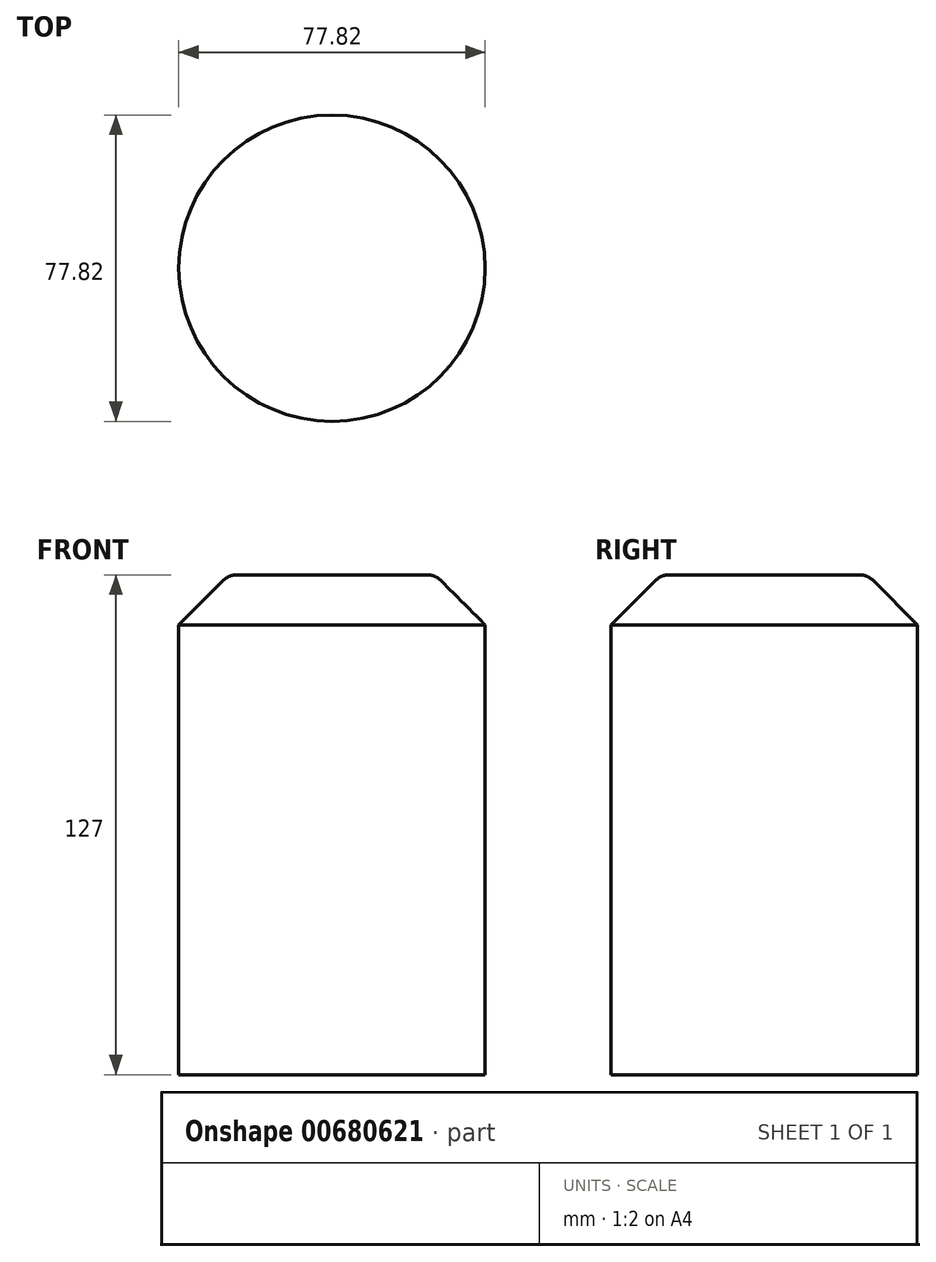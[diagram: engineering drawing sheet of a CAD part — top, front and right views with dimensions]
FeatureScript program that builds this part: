
annotation { "Feature Type Name" : "Feature", "Feature Type Description" : "" }
export const myFeature = defineFeature(function(context is Context, id is Id, definition is map)
    precondition{}
    {
        {
            var Q0;
            Q0=qCreatedBy(makeId("Top.planeOp"),FACE);
            var sketch = newSketch(context, id + "F0", { "sketchPlane" : qUnion([Q0])});
            skCircle(sketch, "E0", {"center": v(0, 0) * mm, "radius": 38.9 * mm});
            skSolve(sketch);
        }
        {
            var Q0;
            Q0=makeQuery(id+"F0.imprint","IMPRINT",FACE,{"disambiguationData":[TD([[makeQuery(id+"F0.imprint","IMPRINT",EDGE,{"derivedFrom":sQuery(id+"F0.wireOp",EDGE,"E0")}),1.0]])]});
            extrude(context, id + "F1", {"entities" : qUnion([Q0]), "depth" : 127 * mm, "offsetDistance" : 25.4 * mm});
        }
        {
            var Q0;
            Q0=makeQuery(id+"F1.opExtrude","CAP_EDGE",EDGE,{"disambiguationData":[OSD([sQuery(id+"F0.wireOp",EDGE,"E0")])],"isStart":false});
            chamfer(context, id + "F2", {"entities" : qUnion([Q0]), "width" : 12.7 * mm, "tangentPropagation" : true});
        }
        {
            var Q0;
            {var subQ0=sQuery(id+"F0.wireOp",EDGE,"E0");Q0=makeQuery(id+"F2.opChamfer","BLEND_EDGE",EDGE,{"blendedFrom":[makeQuery(id+"F1.opExtrude","CAP_EDGE",EDGE,{"disambiguationData":[OSD([subQ0])],"isStart":false}),makeQuery(id+"F1.opExtrude","CAP_FACE",FACE,{"disambiguationData":[OSD([subQ0])],"isStart":false})],"blendedInto":[makeQuery(id+"F1.opExtrude","CAP_FACE",FACE,{"disambiguationData":[OSD([subQ0])],"isStart":false})]});}
            fillet(context, id + "F3", {"entities" : qUnion([Q0]), "radius" : 5.08 * mm, "tangentPropagation" : true, "allowEdgeOverflow" : false});
        }
    });
